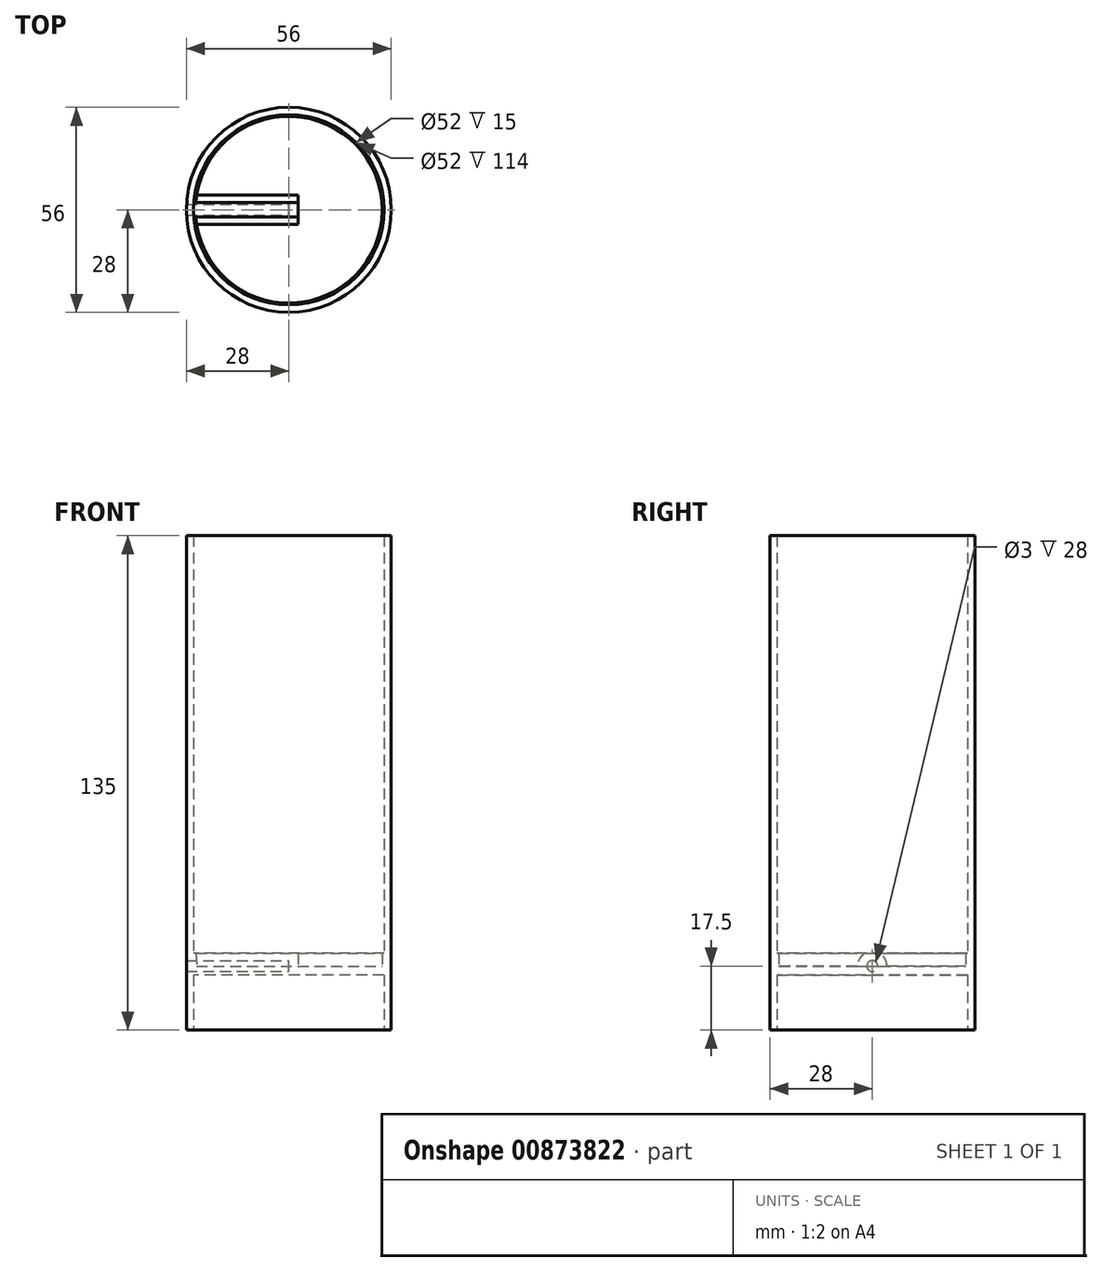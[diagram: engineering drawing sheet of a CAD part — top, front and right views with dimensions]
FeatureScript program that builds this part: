
annotation { "Feature Type Name" : "Feature", "Feature Type Description" : "" }
export const myFeature = defineFeature(function(context is Context, id is Id, definition is map)
    precondition{}
    {
        {
            var Q0;
            Q0=qCreatedBy(makeId("Top.planeOp"),FACE);
            var sketch = newSketch(context, id + "F0", { "sketchPlane" : qUnion([Q0])});
            skCircle(sketch, "E0", {"center": v(0, 0) * mm, "radius": 28 * mm});
            skCircle(sketch, "E1", {"center": v(0, 0) * mm, "radius": 26 * mm});
            skSolve(sketch);
        }
        {
            var Q0;
            Q0=makeQuery(id+"F0.imprint","IMPRINT",FACE,{"disambiguationData":[TD([[makeQuery(id+"F0.imprint","IMPRINT",EDGE,{"derivedFrom":sQuery(id+"F0.wireOp",EDGE,"E1")}),1.0]])]});
            extrude(context, id + "F1", {"entities" : qUnion([Q0]), "depth" : 6 * mm, "offsetDistance" : 25 * mm});
        }
        {
            var Q0;
            Q0 = qSketchRegion(id + "F0", true);
            extrude(context, id + "F2", {"entities" : qUnion([Q0]), "operationType" : NewBodyOperationType.ADD, "depth" : 120 * mm, "offsetDistance" : 25 * mm, "hasSecondDirection" : true, "secondDirectionOppositeDirection" : true, "secondDirectionDepth" : 15 * mm});
        }
        {
            var Q0;
            Q0=qCreatedBy(makeId("Right.planeOp"),FACE);
            var sketch = newSketch(context, id + "F3", { "sketchPlane" : qUnion([Q0])});
            skLineSegment(sketch, "E2", {"start": v(0, 0) * mm, "end": v(0, 2.5) * mm, "construction": true});
            skCircle(sketch, "E3", {"center": v(0, 2.5) * mm, "radius": 1.5 * mm});
            skSolve(sketch);
        }
        {
            var Q0;
            Q0=makeQuery(id+"F3.imprint","IMPRINT",FACE,{"disambiguationData":[TD([[makeQuery(id+"F3.imprint","IMPRINT",EDGE,{"derivedFrom":sQuery(id+"F3.wireOp",EDGE,"E3")}),1.0]])]});
            var Q1;
            Q1=sQuery(id+"F3.wireOp",EDGE,"E3");
            extrude(context, id + "F4", {"entities" : qUnion([Q0]), "operationType" : NewBodyOperationType.REMOVE, "surfaceEntities" : qUnion([Q1]), "oppositeDirection" : true, "depth" : 30 * mm, "offsetDistance" : 25 * mm});
        }
        {
            var Q0;
            Q0=makeQuery(id+"F1.opExtrude","CAP_FACE",FACE,{"disambiguationData":[OSD([sQuery(id+"F0.wireOp",EDGE,"E1")])],"isStart":false});
            shell(context, id + "F5", {"entities" : qUnion([Q0]), "thickness" : 2.5 * mm});
        }
    });
